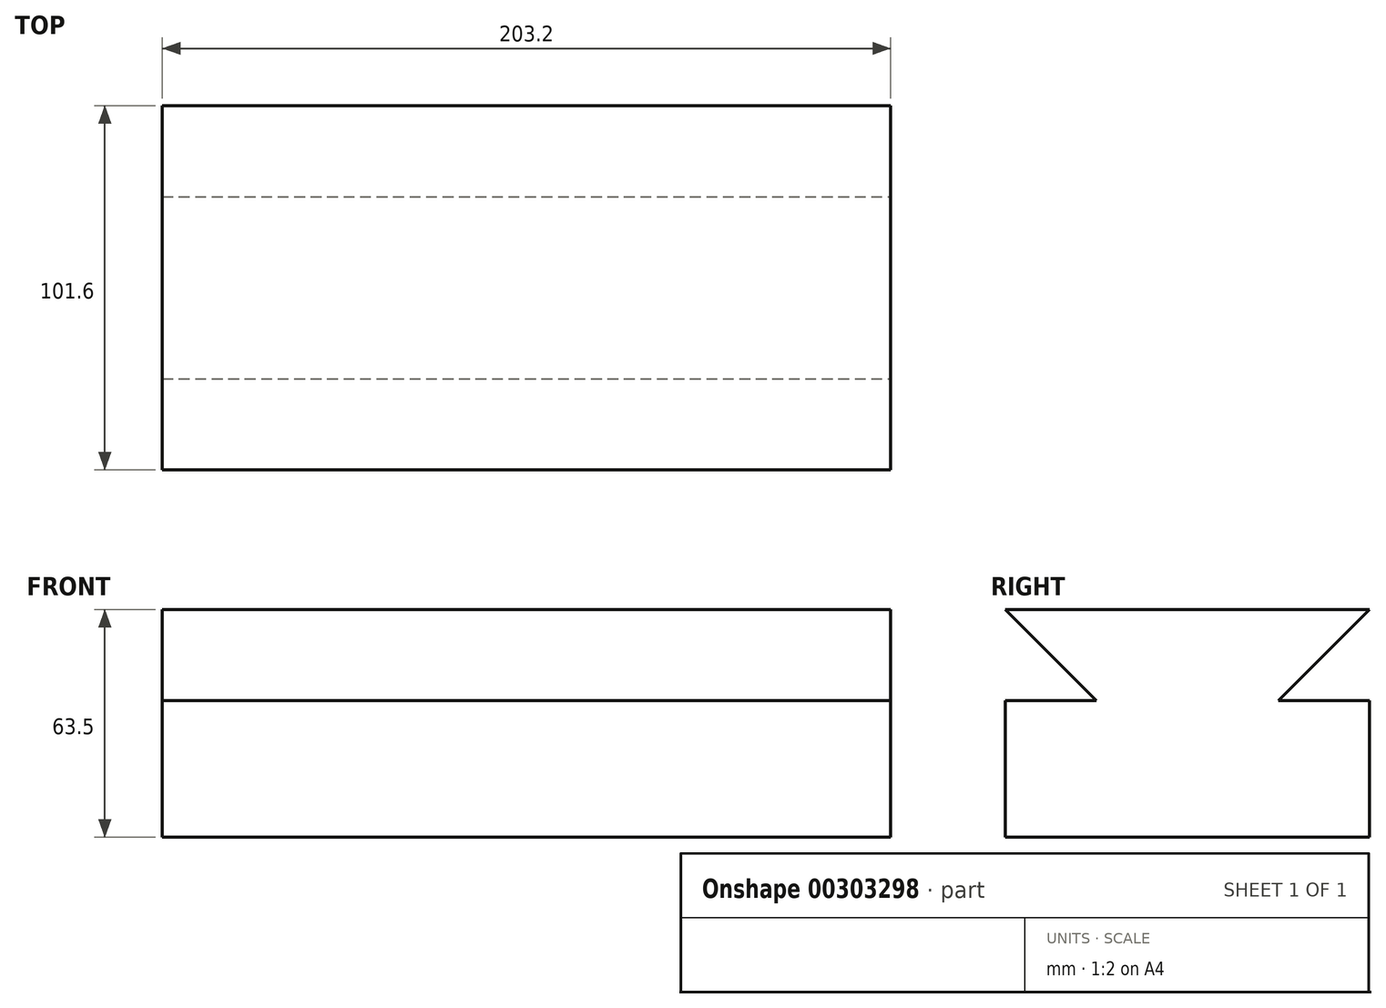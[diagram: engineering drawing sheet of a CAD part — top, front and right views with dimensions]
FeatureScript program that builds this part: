
annotation { "Feature Type Name" : "Feature", "Feature Type Description" : "" }
export const myFeature = defineFeature(function(context is Context, id is Id, definition is map)
    precondition{}
    {
        {
            var Q0;
            Q0=qCreatedBy(makeId("Right.planeOp"),FACE);
            var sketch = newSketch(context, id + "F0", { "sketchPlane" : qUnion([Q0])});
            skLineSegment(sketch, "E0", {"start": v(-26.72, 63.5) * mm, "end": v(-1.32, 38.1) * mm});
            skLineSegment(sketch, "E1", {"start": v(-1.32, 38.1) * mm, "end": v(-26.72, 38.1) * mm});
            skLineSegment(sketch, "E2", {"start": v(74.88, 63.5) * mm, "end": v(49.48, 38.1) * mm});
            skLineSegment(sketch, "E3", {"start": v(49.48, 38.1) * mm, "end": v(74.88, 38.1) * mm});
            skLineSegment(sketch, "E4.bottom", {"start": v(-26.72, 63.5) * mm, "end": v(74.88, 63.5) * mm});
            skLineSegment(sketch, "E4.top", {"start": v(-26.72, 0) * mm, "end": v(74.88, 0) * mm});
            skLineSegment(sketch, "E4.left", {"start": v(-26.72, 63.5) * mm, "end": v(-26.72, 0) * mm});
            skLineSegment(sketch, "E4.right", {"start": v(74.88, 63.5) * mm, "end": v(74.88, 0) * mm});
            skSolve(sketch);
        }
        {
            var Q0;
            Q0=makeQuery(id+"F0.imprint","IMPRINT",FACE,{"disambiguationData":[TD([[makeQuery(id+"F0.imprint","IMPRINT",EDGE,{"derivedFrom":sQuery(id+"F0.wireOp",EDGE,"E0")}),1.0]])]});
            extrude(context, id + "F1", {"entities" : qUnion([Q0]), "oppositeDirection" : true, "depth" : 203.2 * mm, "offsetDistance" : 25.4 * mm});
        }
    });
